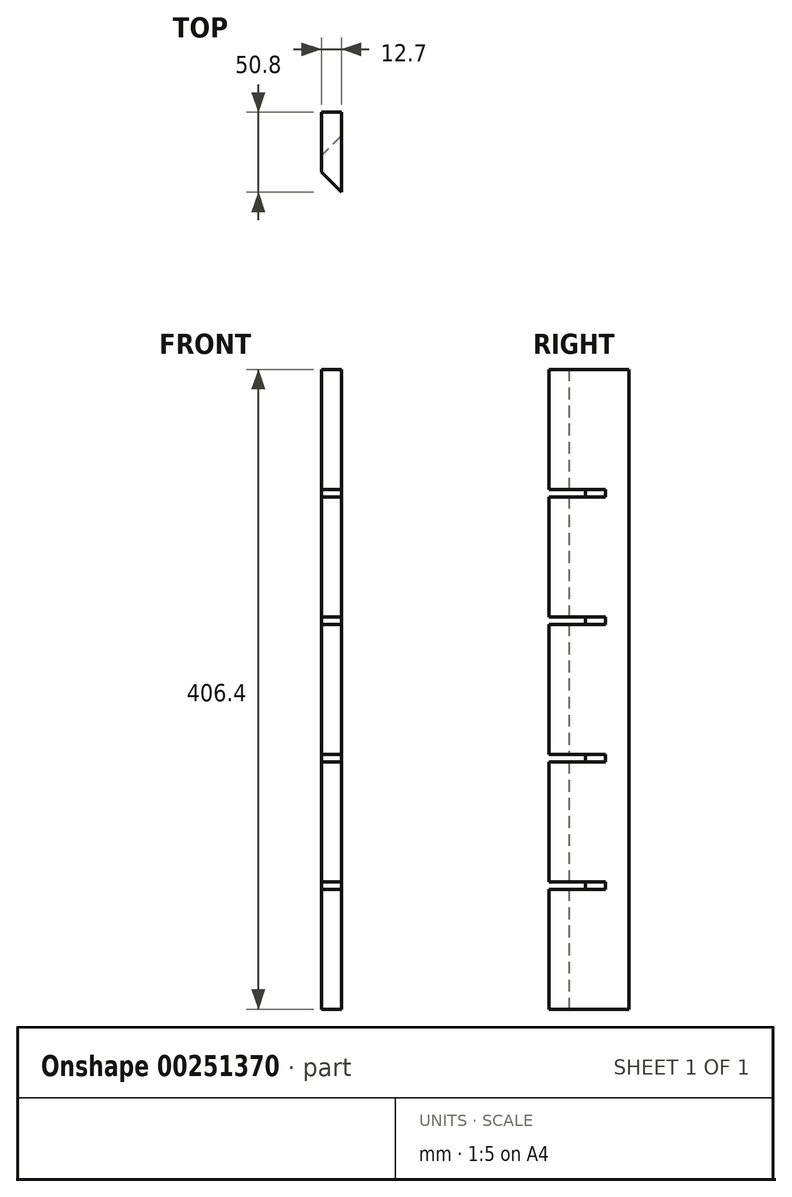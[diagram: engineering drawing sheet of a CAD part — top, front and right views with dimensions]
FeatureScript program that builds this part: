
annotation { "Feature Type Name" : "Feature", "Feature Type Description" : "" }
export const myFeature = defineFeature(function(context is Context, id is Id, definition is map)
    precondition{}
    {
        {
            var Q0;
            Q0=qCreatedBy(makeId("Top.planeOp"),FACE);
            var sketch = newSketch(context, id + "F0", { "sketchPlane" : qUnion([Q0])});
            skLineSegment(sketch, "E0", {"start": v(0, 0) * mm, "end": v(0, 50.8) * mm});
            skLineSegment(sketch, "E1", {"start": v(0, 50.8) * mm, "end": v(-12.7, 50.8) * mm});
            skLineSegment(sketch, "E2", {"start": v(-12.7, 50.8) * mm, "end": v(-12.7, 12.7) * mm});
            skLineSegment(sketch, "E3", {"start": v(0, 0) * mm, "end": v(-12.7, 12.7) * mm});
            skSolve(sketch);
        }
        {
            var Q0;
            Q0 = qSketchRegion(id + "F0", true);
            extrude(context, id + "F1", {"entities" : qUnion([Q0]), "depth" : 457.2 * mm});
        }
        {
            var Q0;
            Q0=makeQuery(id+"F1.opExtrude","CAP_FACE",FACE,{"disambiguationData":[OSD([sQuery(id+"F0.wireOp",EDGE,"E0"),sQuery(id+"F0.wireOp",EDGE,"E1"),sQuery(id+"F0.wireOp",EDGE,"E2"),sQuery(id+"F0.wireOp",EDGE,"E3")])],"isStart":true});
            var Q1;
            Q1=makeQuery(id+"F1.opExtrude","CAP_FACE",FACE,{"disambiguationData":[OSD([sQuery(id+"F0.wireOp",EDGE,"E0"),sQuery(id+"F0.wireOp",EDGE,"E1"),sQuery(id+"F0.wireOp",EDGE,"E2"),sQuery(id+"F0.wireOp",EDGE,"E3")])],"isStart":false});
            extrude(context, id + "F2", {"entities" : qUnion([Q0, Q1]), "operationType" : NewBodyOperationType.REMOVE, "oppositeDirection" : true, "depth" : 50.8 * mm});
        }
        {
            var Q0;
            Q0=makeQuery(id+"F1.opExtrude","SWEPT_FACE",FACE,{"disambiguationData":[OSD([sQuery(id+"F0.wireOp",EDGE,"E3")])]});
            var sketch = newSketch(context, id + "F3", { "sketchPlane" : qUnion([Q0])});
            skLineSegment(sketch, "E4", {"start": v(0, 457.2) * mm, "end": v(0, 381) * mm});
            skLineSegment(sketch, "E5", {"start": v(0, 381) * mm, "end": v(-25.4, 381) * mm});
            skLineSegment(sketch, "E6", {"start": v(-25.4, 381) * mm, "end": v(-25.4, 376.24) * mm});
            skLineSegment(sketch, "E7", {"start": v(-25.4, 376.24) * mm, "end": v(3.23, 376.24) * mm});
            skLineSegment(sketch, "E8", {"start": v(3.23, 376.24) * mm, "end": v(3.23, 381) * mm});
            skLineSegment(sketch, "E9", {"start": v(3.23, 381) * mm, "end": v(0, 381) * mm});
            skLineSegment(sketch, "E10", {"start": v(0, 127) * mm, "end": v(-25.4, 127) * mm});
            skLineSegment(sketch, "E11", {"start": v(-25.4, 127) * mm, "end": v(-25.4, 131.76) * mm});
            skLineSegment(sketch, "E12", {"start": v(-25.4, 131.76) * mm, "end": v(10.67, 131.76) * mm});
            skLineSegment(sketch, "E13", {"start": v(10.67, 131.76) * mm, "end": v(10.67, 127) * mm});
            skLineSegment(sketch, "E14", {"start": v(10.67, 127) * mm, "end": v(0, 127) * mm});
            skLineSegment(sketch, "E15", {"start": v(0, 131.76) * mm, "end": v(0, 207.96) * mm});
            skLineSegment(sketch, "E16", {"start": v(0, 207.96) * mm, "end": v(-25.4, 207.96) * mm});
            skLineSegment(sketch, "E17", {"start": v(-25.4, 207.96) * mm, "end": v(-25.4, 212.73) * mm});
            skLineSegment(sketch, "E18", {"start": v(-25.4, 212.73) * mm, "end": v(8.92, 212.73) * mm});
            skLineSegment(sketch, "E19", {"start": v(8.92, 212.73) * mm, "end": v(8.92, 207.96) * mm});
            skLineSegment(sketch, "E20", {"start": v(8.92, 207.96) * mm, "end": v(0, 207.96) * mm});
            skLineSegment(sketch, "E21", {"start": v(0, 376.24) * mm, "end": v(0, 300.04) * mm});
            skLineSegment(sketch, "E22", {"start": v(0, 300.04) * mm, "end": v(-25.4, 300.04) * mm});
            skLineSegment(sketch, "E23", {"start": v(-25.4, 300.04) * mm, "end": v(-25.4, 295.28) * mm});
            skLineSegment(sketch, "E24", {"start": v(-25.4, 295.28) * mm, "end": v(5.05, 295.28) * mm});
            skLineSegment(sketch, "E25", {"start": v(5.05, 295.28) * mm, "end": v(5.05, 300.04) * mm});
            skLineSegment(sketch, "E26", {"start": v(5.05, 300.04) * mm, "end": v(0, 300.04) * mm});
            skSolve(sketch);
        }
        {
            var Q0;
            Q0 = qSketchRegion(id + "F3", true);
            extrude(context, id + "F4", {"entities" : qUnion([Q0]), "operationType" : NewBodyOperationType.REMOVE, "endBound" : BoundingType.THROUGH_ALL, "oppositeDirection" : true, "depth" : 25.4 * mm});
        }
    });
